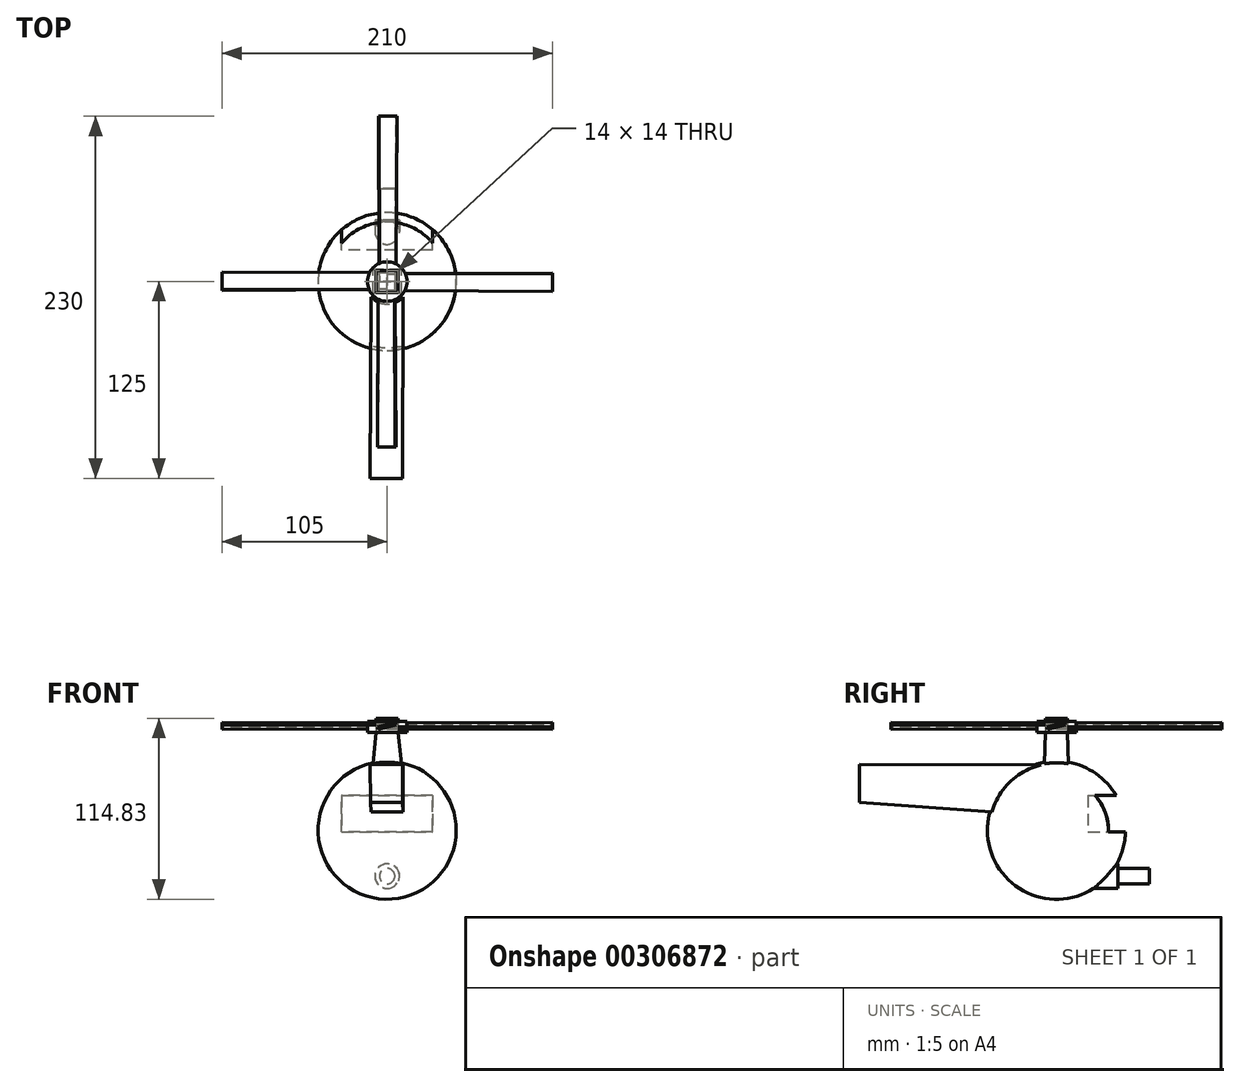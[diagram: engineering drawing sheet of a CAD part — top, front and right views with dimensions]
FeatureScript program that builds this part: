
annotation { "Feature Type Name" : "Feature", "Feature Type Description" : "" }
export const myFeature = defineFeature(function(context is Context, id is Id, definition is map)
    precondition{}
    {
        {
            var Q0;
            Q0=qCreatedBy(makeId("Top.planeOp"),FACE);
            var sketch = newSketch(context, id + "F0", { "sketchPlane" : qUnion([Q0])});
            skArc(sketch, "E0", {"start": v(0, 43.83) * mm, "mid": v(-43.83, 0) * mm, "end": v(0, -43.83) * mm});
            skLineSegment(sketch, "E1", {"start": v(0, 43.83) * mm, "end": v(0, -43.83) * mm});
            skLineSegment(sketch, "E2", {"start": v(0, -43.83) * mm, "end": v(0, 43.83) * mm});
            skSolve(sketch);
        }
        {
            var Q0;
            Q0=makeQuery(id+"F0.imprint","IMPRINT",FACE,{"disambiguationData":[TD([[makeQuery(id+"F0.imprint","IMPRINT",EDGE,{"derivedFrom":sQuery(id+"F0.wireOp",EDGE,"E0")}),1.0]])]});
            var Q1;
            Q1=sQuery(id+"F0.wireOp",EDGE,"E2");
            revolve(context, id + "F1", {"entities" : qUnion([Q0]), "axis" : qUnion([Q1]), "revolveType" : RevolveType.FULL});
        }
        {
            var Q0;
            Q0=qCreatedBy(makeId("Top.planeOp"),FACE);
            var sketch = newSketch(context, id + "F2", { "sketchPlane" : qUnion([Q0])});
            skLineSegment(sketch, "E3.bottom", {"start": v(-13.55, 8.7) * mm, "end": v(13.55, 8.7) * mm});
            skLineSegment(sketch, "E3.top", {"start": v(-13.55, -8.7) * mm, "end": v(13.55, -8.7) * mm});
            skLineSegment(sketch, "E3.left", {"start": v(-13.55, 8.7) * mm, "end": v(-13.55, -8.7) * mm});
            skLineSegment(sketch, "E3.right", {"start": v(13.55, 8.7) * mm, "end": v(13.55, -8.7) * mm});
            skPoint(sketch, "E3.middle", {"position": v(0, 0) * mm});
            skSolve(sketch);
        }
        {
            var Q0;
            Q0=qCreatedBy(makeId("Top.planeOp"),FACE);
            cPlane(context, id + "F3", {"entities" : qUnion([Q0]), "cplaneType" : CPlaneType.OFFSET, "offset" : 62 * mm, "width" : 150 * mm, "height" : 150 * mm});
        }
        {
            var Q0;
            Q0=qCreatedBy(id+"F3.planeOp",FACE);
            var sketch = newSketch(context, id + "F4", { "sketchPlane" : qUnion([Q0])});
            skLineSegment(sketch, "E4.bottom", {"start": v(-7, 7) * mm, "end": v(7, 7) * mm});
            skLineSegment(sketch, "E4.top", {"start": v(-7, -7) * mm, "end": v(7, -7) * mm});
            skLineSegment(sketch, "E4.left", {"start": v(-7, 7) * mm, "end": v(-7, -7) * mm});
            skLineSegment(sketch, "E4.right", {"start": v(7, 7) * mm, "end": v(7, -7) * mm});
            skPoint(sketch, "E4.middle", {"position": v(0, 0) * mm});
            skSolve(sketch);
        }
        {
            var Q1;
            Q1 = qSketchRegion(id + "F2", true);
            var Q2;
            Q2 = qSketchRegion(id + "F4", true);
            loft(context, id + "F5", {"operationType" : NewBodyOperationType.ADD, "sheetProfilesArray" : [{ "sheetProfileEntities" : qUnion([Q1]) }, { "sheetProfileEntities" : qUnion([Q2]) }]});
        }
        {
            var Q0;
            Q0=makeQuery(id+"F5.opLoft","CAP_FACE",FACE,{"disambiguationData":[OSD([makeQuery(id+"F4.imprint","IMPRINT",FACE,{"disambiguationData":[TD([[makeQuery(id+"F4.imprint","IMPRINT",EDGE,{"derivedFrom":sQuery(id+"F4.wireOp",EDGE,"E4.bottom")}),-1.0]])]})])],"isStart":true});
            var sketch = newSketch(context, id + "F6", { "sketchPlane" : qUnion([Q0])});
            skCircle(sketch, "E5", {"center": v(0, 0) * mm, "radius": 12.54 * mm});
            skSolve(sketch);
        }
        {
            var Q0;
            Q0=makeQuery(id+"F6.imprint","IMPRINT",FACE,{"disambiguationData":[TD([[makeQuery(id+"F6.imprint","IMPRINT",EDGE,{"derivedFrom":sQuery(id+"F6.wireOp",EDGE,"E5")}),1.0]])]});
            extrude(context, id + "F7", {"entities" : qUnion([Q0]), "depth" : 7 * mm});
        }
        {
            var Q0;
            Q0=makeQuery(id+"F5.opLoft","CAP_FACE",FACE,{"disambiguationData":[OSD([makeQuery(id+"F4.imprint","IMPRINT",FACE,{"disambiguationData":[TD([[makeQuery(id+"F4.imprint","IMPRINT",EDGE,{"derivedFrom":sQuery(id+"F4.wireOp",EDGE,"E4.bottom")}),-1.0]])]})])],"isStart":true});
            var sketch = newSketch(context, id + "F8", { "sketchPlane" : qUnion([Q0])});
            skLineSegment(sketch, "E6.bottom", {"start": v(-7, 7) * mm, "end": v(7, 7) * mm});
            skLineSegment(sketch, "E6.top", {"start": v(-7, -7) * mm, "end": v(7, -7) * mm});
            skLineSegment(sketch, "E6.left", {"start": v(-7, 7) * mm, "end": v(-7, -7) * mm});
            skLineSegment(sketch, "E6.right", {"start": v(7, 7) * mm, "end": v(7, -7) * mm});
            skPoint(sketch, "E6.middle", {"position": v(0, 0) * mm});
            skSolve(sketch);
        }
        {
            var Q0;
            Q0 = qSketchRegion(id + "F8", true);
            extrude(context, id + "F9", {"entities" : qUnion([Q0]), "depth" : 9 * mm});
        }
        {
            var Q0;
            Q0=qCreatedBy(makeId("Right.planeOp"),FACE);
            cPlane(context, id + "F10", {"entities" : qUnion([Q0]), "cplaneType" : CPlaneType.OFFSET, "offset" : 105 * mm, "width" : 150 * mm, "height" : 150 * mm});
        }
        {
            var Q0;
            Q0=qCreatedBy(makeId("Right.planeOp"),FACE);
            var sketch = newSketch(context, id + "F11", { "sketchPlane" : qUnion([Q0])});
            skLineSegment(sketch, "E7", {"start": v(-5.72, 65.54) * mm, "end": v(4.65, 68.22) * mm});
            skLineSegment(sketch, "E8", {"start": v(4.65, 68.22) * mm, "end": v(4.96, 67.04) * mm});
            skLineSegment(sketch, "E9", {"start": v(4.96, 67.04) * mm, "end": v(-5.35, 64.38) * mm});
            skLineSegment(sketch, "E10", {"start": v(-5.35, 64.38) * mm, "end": v(-5.72, 65.54) * mm});
            skSolve(sketch);
        }
        {
            var Q0;
            Q0=qCreatedBy(id+"F10.planeOp",FACE);
            var sketch = newSketch(context, id + "F12", { "sketchPlane" : qUnion([Q0])});
            skLineSegment(sketch, "E11", {"start": v(-6.19, 65.48) * mm, "end": v(5.15, 68.42) * mm});
            skLineSegment(sketch, "E12", {"start": v(5.15, 68.42) * mm, "end": v(5.56, 66.85) * mm});
            skLineSegment(sketch, "E13", {"start": v(5.56, 66.85) * mm, "end": v(-5.72, 63.93) * mm});
            skLineSegment(sketch, "E14", {"start": v(-5.72, 63.93) * mm, "end": v(-6.19, 65.48) * mm});
            skSolve(sketch);
        }
        {
            var Q0;
            Q0 = qSketchRegion(id + "F11", true);
            var Q1;
            Q1 = qSketchRegion(id + "F12", true);
            loft(context, id + "F13", {"sheetProfilesArray" : [{ "sheetProfileEntities" : qUnion([Q0]) }, { "sheetProfileEntities" : qUnion([Q1]) }]});
        }
        {
            var Q0;
            Q0=makeQuery(id+"F13.opLoft","SWEPT_BODY",BODY,{"disambiguationData":[OSD([makeQuery(id+"F11.imprint","IMPRINT",FACE,{"disambiguationData":[TD([[makeQuery(id+"F11.imprint","IMPRINT",EDGE,{"derivedFrom":sQuery(id+"F11.wireOp",EDGE,"E7")}),-1.0]])]}),makeQuery(id+"F12.imprint","IMPRINT",FACE,{"disambiguationData":[TD([[makeQuery(id+"F12.imprint","IMPRINT",EDGE,{"derivedFrom":sQuery(id+"F12.wireOp",EDGE,"E11")}),-1.0]])]})])]});
            var Q1;
            Q1=makeQuery(id+"F7.opExtrude","SWEPT_FACE",FACE,{"disambiguationData":[OSD([sQuery(id+"F6.wireOp",EDGE,"E5")])]});
            circularPattern(context, id + "F14", {"entities" : qUnion([Q0]), "axis" : qUnion([Q1]), "angle" : 360 * degree, "instanceCount" : 4, "equalSpace" : true});
        }
        {
            var Q0;
            Q0=qCreatedBy(makeId("Front.planeOp"),FACE);
            var sketch = newSketch(context, id + "F15", { "sketchPlane" : qUnion([Q0])});
            skLineSegment(sketch, "E15.bottom", {"start": v(-10.23, 41.42) * mm, "end": v(10.23, 41.42) * mm});
            skLineSegment(sketch, "E15.top", {"start": v(-10.23, 8.7) * mm, "end": v(10.23, 8.7) * mm});
            skLineSegment(sketch, "E15.left", {"start": v(-10.23, 41.42) * mm, "end": v(-10.23, 8.7) * mm});
            skLineSegment(sketch, "E15.right", {"start": v(10.23, 41.42) * mm, "end": v(10.23, 8.7) * mm});
            skPoint(sketch, "E15.middle", {"position": v(0, 25.06) * mm});
            skSolve(sketch);
        }
        {
            var Q0;
            Q0=qCreatedBy(makeId("Front.planeOp"),FACE);
            cPlane(context, id + "F16", {"entities" : qUnion([Q0]), "cplaneType" : CPlaneType.OFFSET, "offset" : 125 * mm, "width" : 150 * mm, "height" : 150 * mm});
        }
        {
            var Q0;
            Q0=qCreatedBy(id+"F16.planeOp",FACE);
            var sketch = newSketch(context, id + "F17", { "sketchPlane" : qUnion([Q0])});
            skLineSegment(sketch, "E16", {"start": v(-10.74, 41.68) * mm, "end": v(9.72, 41.68) * mm});
            skLineSegment(sketch, "E17", {"start": v(9.72, 41.68) * mm, "end": v(9.72, 17.64) * mm});
            skLineSegment(sketch, "E18", {"start": v(9.72, 17.64) * mm, "end": v(-10.48, 17.64) * mm});
            skLineSegment(sketch, "E19", {"start": v(-10.48, 17.64) * mm, "end": v(-10.74, 41.68) * mm});
            skSolve(sketch);
        }
        {
            var Q1;
            Q1 = qSketchRegion(id + "F17", true);
            var Q2;
            Q2 = qSketchRegion(id + "F15", true);
            loft(context, id + "F18", {"operationType" : NewBodyOperationType.ADD, "sheetProfilesArray" : [{ "sheetProfileEntities" : qUnion([Q1]) }, { "sheetProfileEntities" : qUnion([Q2]) }]});
        }
        {
            var Q0;
            Q0=qCreatedBy(makeId("Front.planeOp"),FACE);
            cPlane(context, id + "F19", {"entities" : qUnion([Q0]), "cplaneType" : CPlaneType.OFFSET, "offset" : 25 * mm, "oppositeDirection" : true, "width" : 150 * mm, "height" : 150 * mm});
        }
        {
            var Q0;
            Q0=qCreatedBy(makeId("Front.planeOp"),FACE);
            cPlane(context, id + "F20", {"entities" : qUnion([Q0]), "cplaneType" : CPlaneType.OFFSET, "offset" : 55 * mm, "oppositeDirection" : true, "width" : 150 * mm, "height" : 150 * mm});
        }
        {
            var Q0;
            Q0=qCreatedBy(id+"F20.planeOp",FACE);
            var sketch = newSketch(context, id + "F21", { "sketchPlane" : qUnion([Q0])});
            skLineSegment(sketch, "E20.bottom", {"start": v(28.9, 21.99) * mm, "end": v(-28.9, 21.99) * mm});
            skLineSegment(sketch, "E20.top", {"start": v(28.9, -1.02) * mm, "end": v(-28.9, -1.02) * mm});
            skLineSegment(sketch, "E20.left", {"start": v(28.9, 21.99) * mm, "end": v(28.9, -1.02) * mm});
            skLineSegment(sketch, "E20.right", {"start": v(-28.9, 21.99) * mm, "end": v(-28.9, -1.02) * mm});
            skPoint(sketch, "E20.middle", {"position": v(0, 10.48) * mm});
            skSolve(sketch);
        }
        {
            var Q0;
            Q0=makeQuery(id+"F21.imprint","IMPRINT",FACE,{"disambiguationData":[TD([[makeQuery(id+"F21.imprint","IMPRINT",EDGE,{"derivedFrom":sQuery(id+"F21.wireOp",EDGE,"E20.bottom")}),1.0]])]});
            extrude(context, id + "F22", {"entities" : qUnion([Q0]), "operationType" : NewBodyOperationType.REMOVE, "depth" : 35 * mm});
        }
        {
            var Q0;
            Q0=qCreatedBy(id+"F20.planeOp",FACE);
            cPlane(context, id + "F23", {"entities" : qUnion([Q0]), "cplaneType" : CPlaneType.OFFSET, "offset" : 45 * mm, "width" : 150 * mm, "height" : 150 * mm});
        }
        {
            var Q0;
            Q0=qCreatedBy(id+"F23.planeOp",FACE);
            var sketch = newSketch(context, id + "F24", { "sketchPlane" : qUnion([Q0])});
            skCircle(sketch, "E21", {"center": v(0, -29.15) * mm, "radius": 7.8 * mm});
            skSolve(sketch);
        }
        {
            var Q0;
            Q0 = qSketchRegion(id + "F24", true);
            var Q1;
            Q1=sQuery(id+"F24.wireOp",EDGE,"E21");
            extrude(context, id + "F25", {"entities" : qUnion([Q0]), "operationType" : NewBodyOperationType.ADD, "surfaceEntities" : qUnion([Q1]), "oppositeDirection" : true, "depth" : 29 * mm});
        }
        {
            var Q0;
            Q0=makeQuery(id+"F25.opExtrude","CAP_FACE",FACE,{"disambiguationData":[OSD([sQuery(id+"F24.wireOp",EDGE,"E21")])],"isStart":false});
            var sketch = newSketch(context, id + "F26", { "sketchPlane" : qUnion([Q0])});
            skCircle(sketch, "E22", {"center": v(0, -29.15) * mm, "radius": 4.88 * mm});
            skSolve(sketch);
        }
        {
            var Q0;
            Q0=makeQuery(id+"F26.imprint","IMPRINT",FACE,{"disambiguationData":[TD([[makeQuery(id+"F26.imprint","IMPRINT",EDGE,{"derivedFrom":sQuery(id+"F26.wireOp",EDGE,"E22")}),1.0]])]});
            var Q1;
            Q1=sQuery(id+"F26.wireOp",EDGE,"E22");
            extrude(context, id + "F27", {"entities" : qUnion([Q0]), "surfaceEntities" : qUnion([Q1]), "depth" : 20 * mm});
        }
    });
